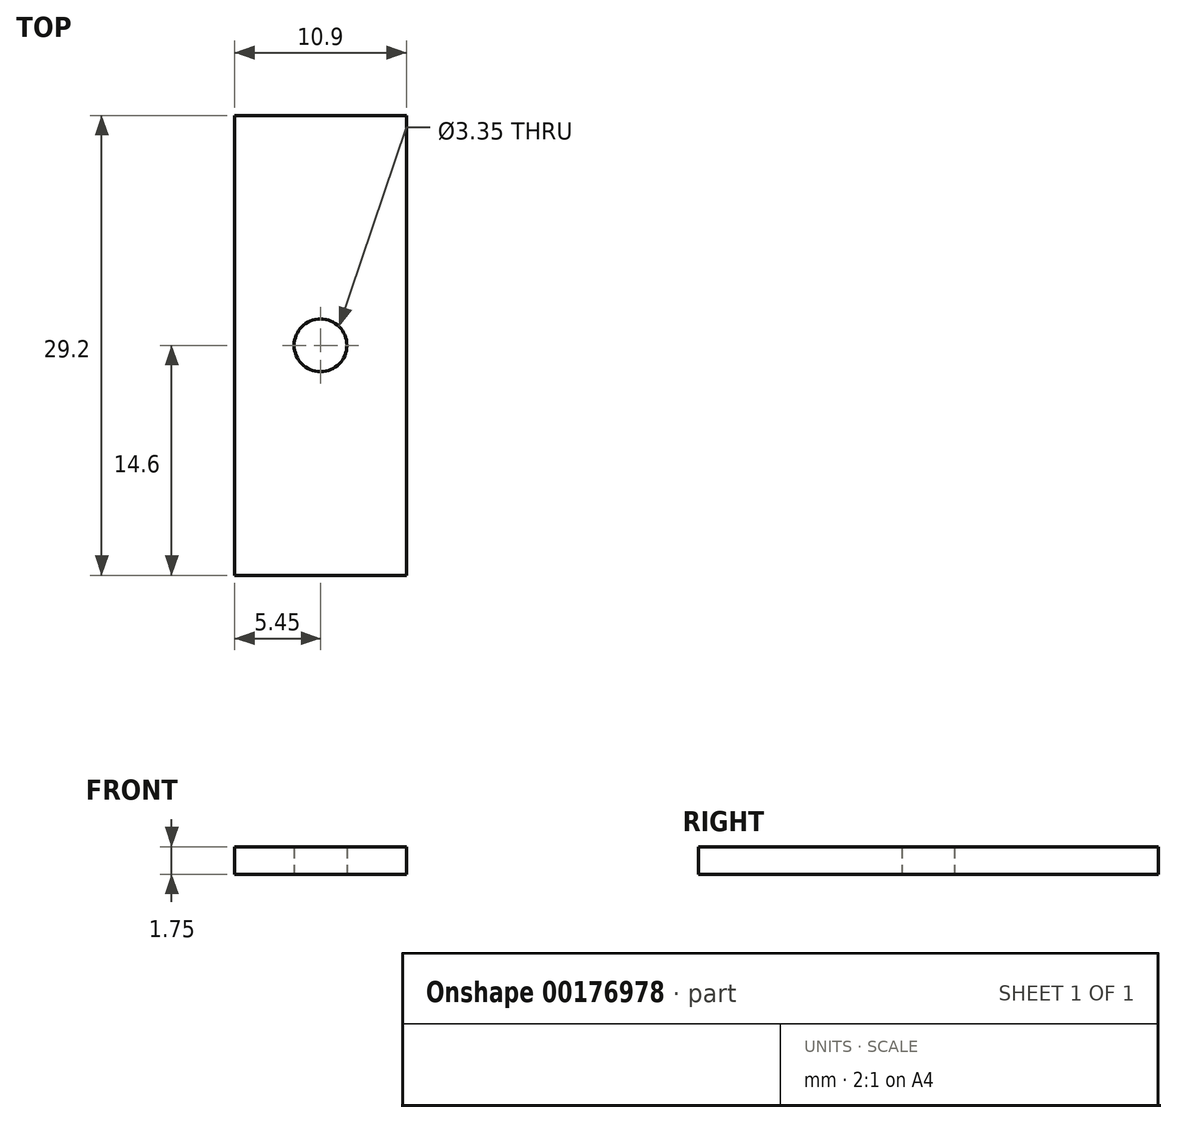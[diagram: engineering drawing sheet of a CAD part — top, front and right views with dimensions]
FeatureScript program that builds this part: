
annotation { "Feature Type Name" : "Feature", "Feature Type Description" : "" }
export const myFeature = defineFeature(function(context is Context, id is Id, definition is map)
    precondition{}
    {
        {
            var Q0;
            Q0=qCreatedBy(makeId("Top.planeOp"),FACE);
            var sketch = newSketch(context, id + "F0", { "sketchPlane" : qUnion([Q0])});
            skLineSegment(sketch, "E0.bottom", {"start": v(5.45, -14.6) * mm, "end": v(-5.45, -14.6) * mm});
            skLineSegment(sketch, "E0.top", {"start": v(5.45, 14.6) * mm, "end": v(-5.45, 14.6) * mm});
            skLineSegment(sketch, "E0.left", {"start": v(5.45, -14.6) * mm, "end": v(5.45, 14.6) * mm});
            skLineSegment(sketch, "E0.right", {"start": v(-5.45, -14.6) * mm, "end": v(-5.45, 14.6) * mm});
            skPoint(sketch, "E0.middle", {"position": v(0, 0) * mm});
            skCircle(sketch, "E1", {"center": v(0, 0) * mm, "radius": 1.68 * mm});
            skSolve(sketch);
        }
        {
            var Q0;
            Q0=makeQuery(id+"F0.imprint","IMPRINT",FACE,{"disambiguationData":[TD([[makeQuery(id+"F0.imprint","IMPRINT",EDGE,{"derivedFrom":sQuery(id+"F0.wireOp",EDGE,"E0.bottom")}),-1.0]])]});
            extrude(context, id + "F1", {"entities" : qUnion([Q0]), "depth" : 1.75 * mm, "offsetDistance" : 25 * mm});
        }
    });
